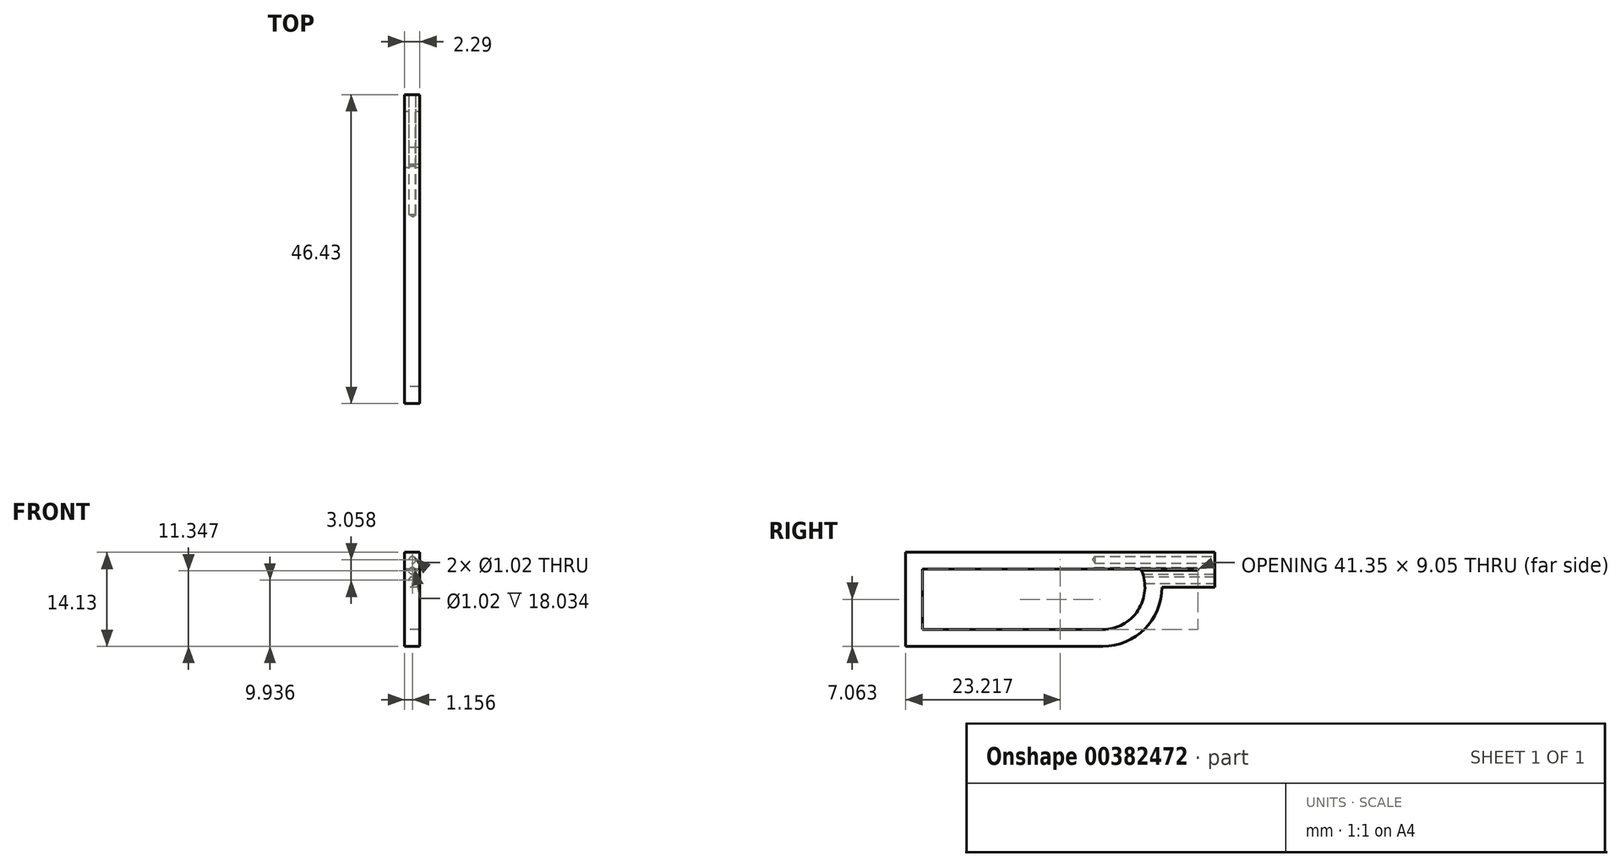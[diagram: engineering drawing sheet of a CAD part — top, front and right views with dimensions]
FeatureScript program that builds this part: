
annotation { "Feature Type Name" : "Feature", "Feature Type Description" : "" }
export const myFeature = defineFeature(function(context is Context, id is Id, definition is map)
    precondition{}
    {
        {
            var Q0;
            Q0=qCreatedBy(makeId("Right.planeOp"),FACE);
            var sketch = newSketch(context, id + "F0", { "sketchPlane" : qUnion([Q0])});
            skLineSegment(sketch, "E0.bottom", {"start": v(-74.14, 8.34) * mm, "end": v(-35.65, 8.34) * mm});
            skLineSegment(sketch, "E0.top", {"start": v(-74.14, -5.8) * mm, "end": v(-44.54, -5.8) * mm});
            skLineSegment(sketch, "E0.left", {"start": v(-74.14, 8.34) * mm, "end": v(-74.14, -5.8) * mm});
            skLineSegment(sketch, "E0.right", {"start": v(-35.65, 8.34) * mm, "end": v(-35.65, 3.1) * mm});
            skPoint(sketch, "E1.visualSharp", {"position": v(-35.65, -5.8) * mm});
            skArc(sketch, "E1.filletArc", {"start": v(-44.54, -5.8) * mm, "mid": v(-38.25, -3.19) * mm, "end": v(-35.65, 3.1) * mm});
            skPoint(sketch, "E2", {"position": v(-74.14, 1.27) * mm});
            skLineSegment(sketch, "E3", {"start": v(-35.65, 8.34) * mm, "end": v(-27.7, 8.34) * mm});
            skLineSegment(sketch, "E4", {"start": v(-27.7, 8.34) * mm, "end": v(-35.65, 3.1) * mm});
            skLineSegment(sketch, "E5", {"start": v(-27.7, 3.1) * mm, "end": v(-35.65, 3.1) * mm});
            skLineSegment(sketch, "E6", {"start": v(-27.7, 8.34) * mm, "end": v(-27.7, 3.1) * mm});
            skSolve(sketch);
        }
        {
            var Q0;
            Q0=makeQuery(id+"F0.imprint","IMPRINT",FACE,{"disambiguationData":[TD([[makeQuery(id+"F0.imprint","IMPRINT",EDGE,{"derivedFrom":sQuery(id+"F0.wireOp",EDGE,"E0.bottom")}),-1.0]])]});
            var Q1;
            Q1=makeQuery(id+"F0.imprint","IMPRINT",FACE,{"disambiguationData":[TD([[makeQuery(id+"F0.imprint","IMPRINT",EDGE,{"derivedFrom":sQuery(id+"F0.wireOp",EDGE,"E4")}),1.0]])]});
            var Q2;
            Q2=makeQuery(id+"F0.imprint","IMPRINT",FACE,{"disambiguationData":[TD([[makeQuery(id+"F0.imprint","IMPRINT",EDGE,{"derivedFrom":sQuery(id+"F0.wireOp",EDGE,"E0.right")}),1.0]])]});
            extrude(context, id + "F1", {"entities" : qUnion([Q0, Q1, Q2]), "depth" : 2.3 * mm});
        }
        {
            var Q0;
            Q0=makeQuery(id+"F1.opExtrude","CAP_FACE",FACE,{"disambiguationData":[OSD([sQuery(id+"F0.wireOp",EDGE,"E0.bottom"),sQuery(id+"F0.wireOp",EDGE,"E0.top"),sQuery(id+"F0.wireOp",EDGE,"E0.left"),sQuery(id+"F0.wireOp",EDGE,"E0.right"),sQuery(id+"F0.wireOp",EDGE,"E1.filletArc")])],"isStart":false});
            var Q1;
            Q1=makeQuery(id+"F1.opExtrude","CAP_FACE",FACE,{"disambiguationData":[OSD([sQuery(id+"F0.wireOp",EDGE,"E0.bottom"),sQuery(id+"F0.wireOp",EDGE,"E0.top"),sQuery(id+"F0.wireOp",EDGE,"E0.left"),sQuery(id+"F0.wireOp",EDGE,"E0.right"),sQuery(id+"F0.wireOp",EDGE,"E1.filletArc")])],"isStart":true});
            shell(context, id + "F2", {"entities" : qUnion([Q0, Q1]), "thickness" : 2.54 * mm});
        }
        {
            var Q0;
            Q0=makeQuery(id+"F1.opExtrude","SWEPT_FACE",FACE,{"disambiguationData":[OSD([sQuery(id+"F0.wireOp",EDGE,"E6")])]});
            var sketch = newSketch(context, id + "F3", { "sketchPlane" : qUnion([Q0])});
            skPoint(sketch, "E7", {"position": v(-1.16, 7.2) * mm});
            skPoint(sketch, "E8", {"position": v(-1.16, 5.56) * mm});
            skPoint(sketch, "E9", {"position": v(-1.16, 4.15) * mm});
            skSolve(sketch);
        }
        {
            var Q0;
            Q0=sQuery(id+"F3.wireOp",VERTEX,"E7");
            var Q1;
            Q1=sQuery(id+"F3.wireOp",VERTEX,"E8");
            var Q2;
            Q2=sQuery(id+"F3.wireOp",VERTEX,"E9");
            var Q3;
            Q3=makeQuery(id+"F1.opExtrude","SWEPT_BODY",BODY,{"disambiguationData":[OSD([sQuery(id+"F0.wireOp",EDGE,"E0.bottom"),sQuery(id+"F0.wireOp",EDGE,"E0.top"),sQuery(id+"F0.wireOp",EDGE,"E0.left"),sQuery(id+"F0.wireOp",EDGE,"E1.filletArc"),sQuery(id+"F0.wireOp",EDGE,"E3"),sQuery(id+"F0.wireOp",EDGE,"E5"),sQuery(id+"F0.wireOp",EDGE,"E6")])]});
            hole(context, id + "F4", {"style" : HoleStyle.SIMPLE, "endStyle" : HoleEndStyle.BLIND, "holeDiameter" : 1.02 * mm, "holeDepth" : 18.03 * mm, "isTappedThrough" : true, "tappedDepth" : 12.7 * mm, "tapClearance" : 3, "startFromSketch" : true, "locations" : qUnion([Q0, Q1, Q2]), "scope" : qUnion([Q3])});
        }
    });
